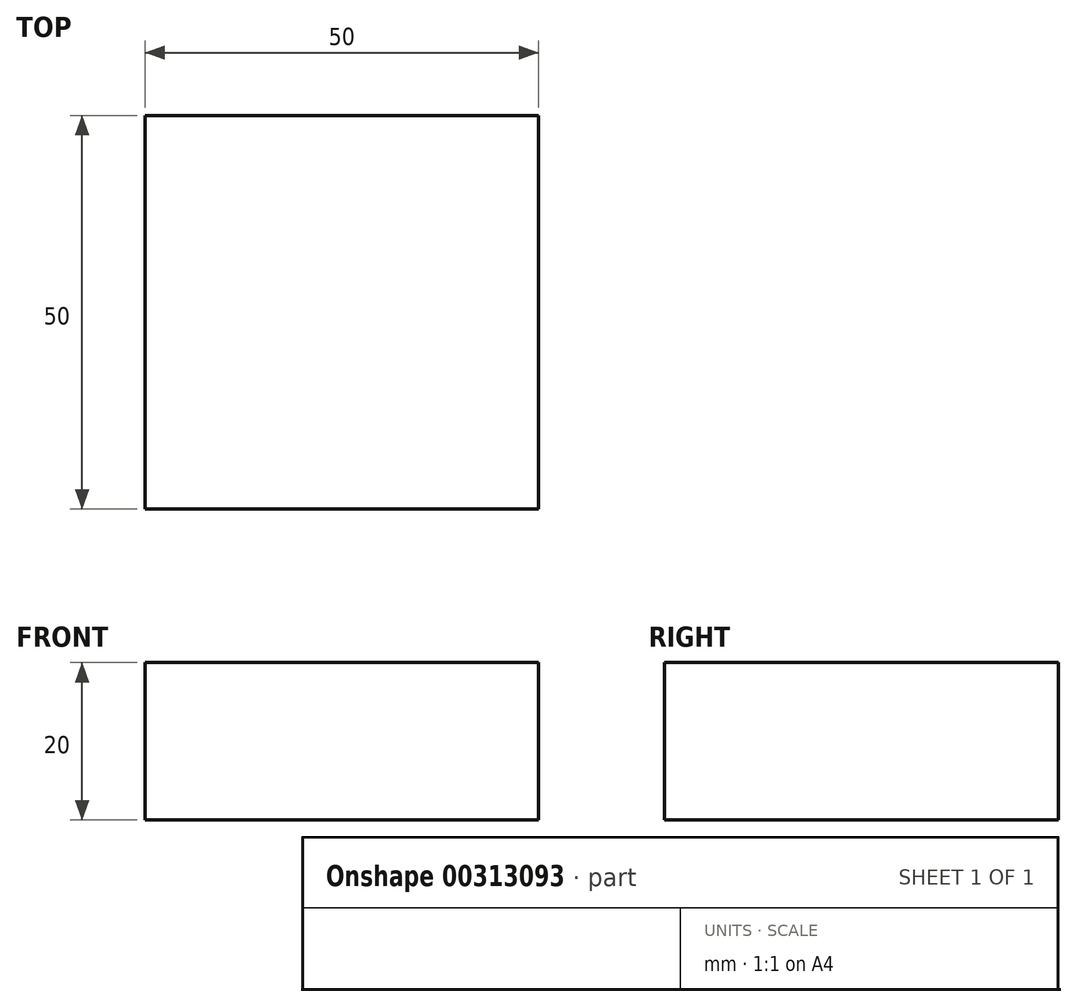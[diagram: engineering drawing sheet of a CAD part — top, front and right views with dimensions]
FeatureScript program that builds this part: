
annotation { "Feature Type Name" : "Feature", "Feature Type Description" : "" }
export const myFeature = defineFeature(function(context is Context, id is Id, definition is map)
    precondition{}
    {
        {
            var Q0;
            Q0=qCreatedBy(makeId("Top.planeOp"),FACE);
            var sketch = newSketch(context, id + "F0", { "sketchPlane" : qUnion([Q0])});
            skLineSegment(sketch, "E0.bottom", {"start": v(25, 25) * mm, "end": v(-25, 25) * mm});
            skLineSegment(sketch, "E0.top", {"start": v(25, -25) * mm, "end": v(-25, -25) * mm});
            skLineSegment(sketch, "E0.left", {"start": v(25, 25) * mm, "end": v(25, -25) * mm});
            skLineSegment(sketch, "E0.right", {"start": v(-25, 25) * mm, "end": v(-25, -25) * mm});
            skPoint(sketch, "E0.middle", {"position": v(0, 0) * mm});
            skSolve(sketch);
        }
        {
            var Q0;
            Q0 = qSketchRegion(id + "F0", true);
            extrude(context, id + "F1", {"entities" : qUnion([Q0]), "endBound" : BoundingType.SYMMETRIC, "depth" : 20 * mm});
        }
    });
